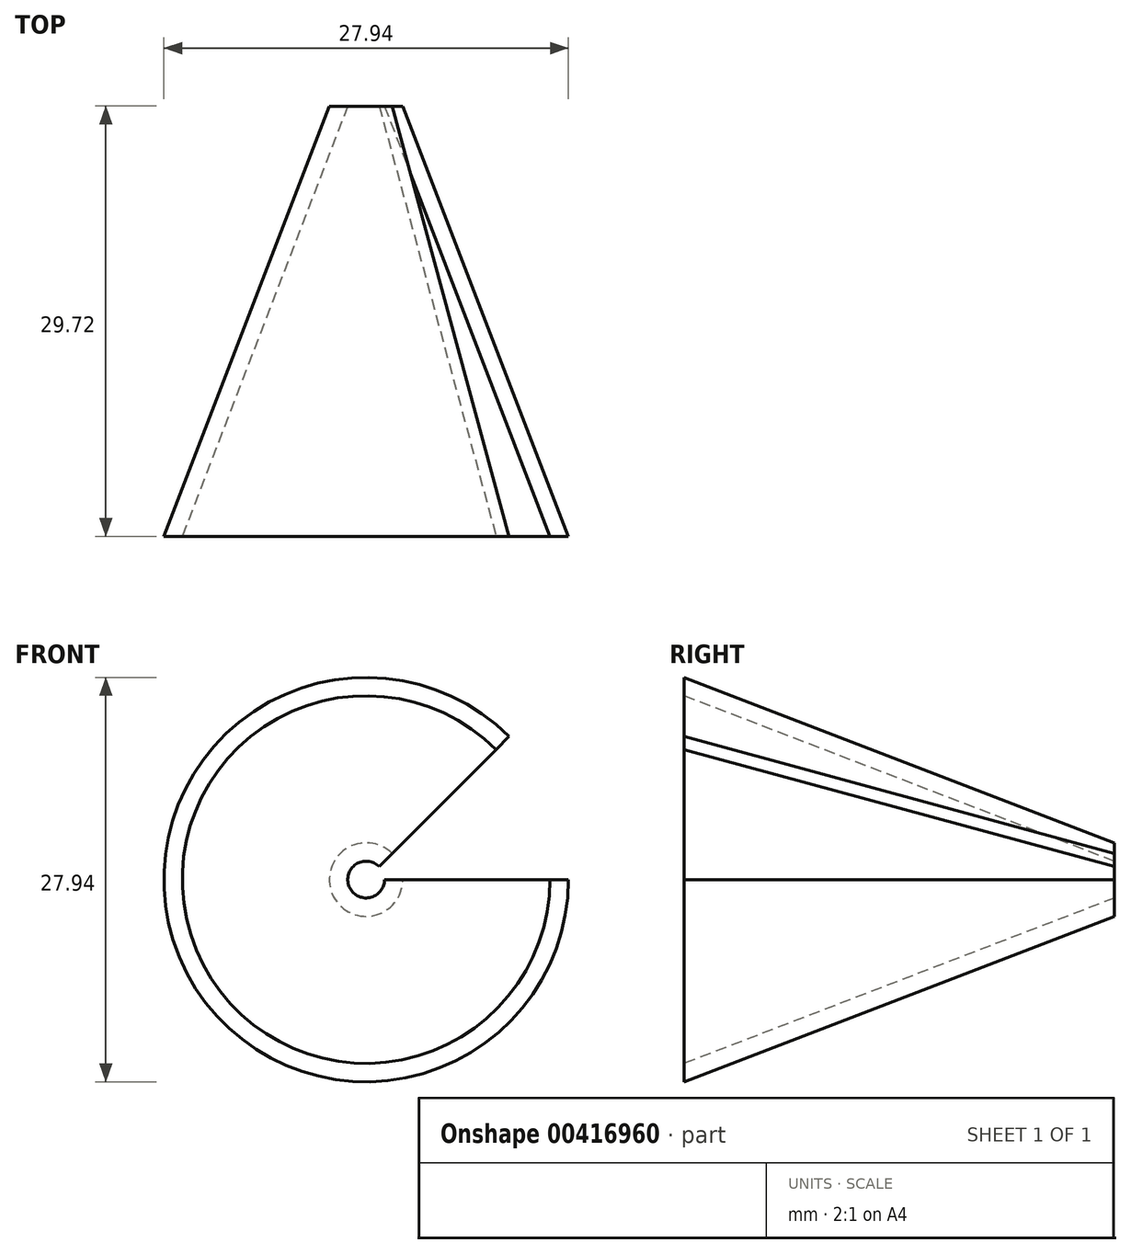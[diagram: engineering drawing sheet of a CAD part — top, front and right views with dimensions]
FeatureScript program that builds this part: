
annotation { "Feature Type Name" : "Feature", "Feature Type Description" : "" }
export const myFeature = defineFeature(function(context is Context, id is Id, definition is map)
    precondition{}
    {
        {
            var Q0;
            Q0=qCreatedBy(makeId("Top.planeOp"),FACE);
            var sketch = newSketch(context, id + "F0", { "sketchPlane" : qUnion([Q0])});
            skLineSegment(sketch, "E0", {"start": v(0, 0) * mm, "end": v(0, 33.02) * mm, "construction": true});
            skLineSegment(sketch, "E1", {"start": v(0, 33.02) * mm, "end": v(12.7, 0) * mm, "construction": true});
            skLineSegment(sketch, "E2", {"start": v(1.27, 29.72) * mm, "end": v(12.7, 0) * mm});
            skLineSegment(sketch, "E3", {"start": v(13.97, 0) * mm, "end": v(2.54, 29.72) * mm});
            skLineSegment(sketch, "E4", {"start": v(2.54, 29.72) * mm, "end": v(1.27, 29.72) * mm});
            skLineSegment(sketch, "E5", {"start": v(13.97, 0) * mm, "end": v(12.7, 0) * mm});
            skSolve(sketch);
        }
        {
            var Q0;
            Q0=makeQuery(id+"F0.imprint","IMPRINT",FACE,{"disambiguationData":[TD([[makeQuery(id+"F0.imprint","IMPRINT",EDGE,{"derivedFrom":sQuery(id+"F0.wireOp",EDGE,"E2")}),1.0]])]});
            var Q1;
            Q1=sQuery(id+"F0.wireOp",EDGE,"E0");
            revolve(context, id + "F1", {"entities" : qUnion([Q0]), "axis" : qUnion([Q1]), "revolveType" : RevolveType.ONE_DIRECTION, "angle" : 315 * degree});
        }
    });
